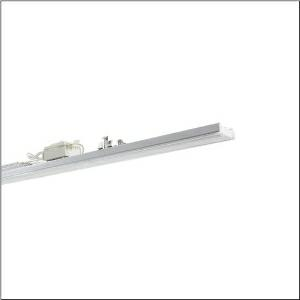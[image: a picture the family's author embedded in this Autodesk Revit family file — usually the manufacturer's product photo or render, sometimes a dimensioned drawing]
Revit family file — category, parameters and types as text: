
# Revit family: licross_11_recessed_ho_51tl12mv4hxm
name_source: partatom
category: Lighting Fixtures
units: mm (PartAtom-declared; Revit-internal decimal feet)

## family parameters
Cut with Voids When Loaded = No
Host = Face
Light Source = No
Part Type = Normal
Room Calculation Point = No
Round Connector Dimension = Use Diameter
Shared = No

## types (1)
- --- (1 x LED, 17260 lm, 89.2 W, 4000K)
    Apparent Load = 89 VA
    CIE Flux Codes = 66 91 98 100 100
    Color Rendering = 80
    Color Temperature = 4000K
    Default Elevation = 1800 mm
    Description = Licross 11 Recessed HO, luminaire insert, of sheet steel, coil coated, white, length: 2.250mm, width: 66mm, height: 67mm, LED rated luminous flux: 17.270lm, light colour: 840, SDCM (Standard Deviation of Colour Matching)MacAdam ≤ 2 SDCM (initial), control gear: ON/OFF Multilumen, with plug, 3-pole, with phase selection, mains connection: 220..240V, AC, 50/60Hz, rated input power: 89W, internal wiring halogen-free, primary optical cover: cover, of PMMA, light emission: direct distribution, primary light characteristic: symmetric, protection rating (complete): IP40, insulation class (complete): insulation class I (protective earthing), certification: CE, ENEC, VDE, UKCA, protection symbol: D if used in an environment without relevant dust loads with corresponding accessories, impact resistance: IK06, permissible ambient temperature for indoor applications: -35..+35°C, corresponds to IFS (International Featured Standards) requirements for safety and quality in the food industry, reducing of maximum allowable ambient temperature of 5°C with ceiling mounting, LABS conformity tested according to VDMA 24364:2018-05, The light source and the operating device comply with the requirements of the Ecodesign Regulation (EU) 2019/2020 and are replaceable in accordance with this regulation, packaging unit: 1 piece
    Height = 58 mm
    Lamp = 1 x LED
    Lamp Light Flux = 17260 lm
    Lamp Power = 89.2 W
    Lamp count = 1
    Length = 2250 mm
    Luminous efficacy = 194 lm/W
    Manufacturer = Siteco
    ModVariant = No
    Model = 51TL12MV4HXM
    Mounting Place = Ceiling
    Mounting Type = Pendant
    Number of Poles = 1
    OnlyDefault = Yes
    Power Factor = 1
    Product Name = Licross 11 Recessed HO
    Product group = luminaire insert | ceiling pendant
    ProductGroupID = 901
    Protection Class = Protection class I
    Protection Degree = IP 40
    RLX_Detail_Level = 1
    RLX_Emergency_Light_Flux = 0 lm
    RLX_Emergency_Type = 0
    RLX_Emergency_Type_DB = No
    RlxData = <blob elided: 27205 chars, md5=1038dfd9>
    Socket = socket
    Standby Power = 0 W
    System Light Flux = 17260 lm
    System Power = 89 W
    Type Comments = factory setting: luminous flux: 100 % | (A | C | E) | 210 mA
    Type Image = l_1296930.jpg
    URL = http://relux.com
    VarID = @adj_089895
    Voltage = 0 V
    Weight = 0.00 kg
    Width = 66 mm

## geometry (parser evidence)
native form markers: Blend x4, Sweep x9
no freeform markers — native parametric forms only
